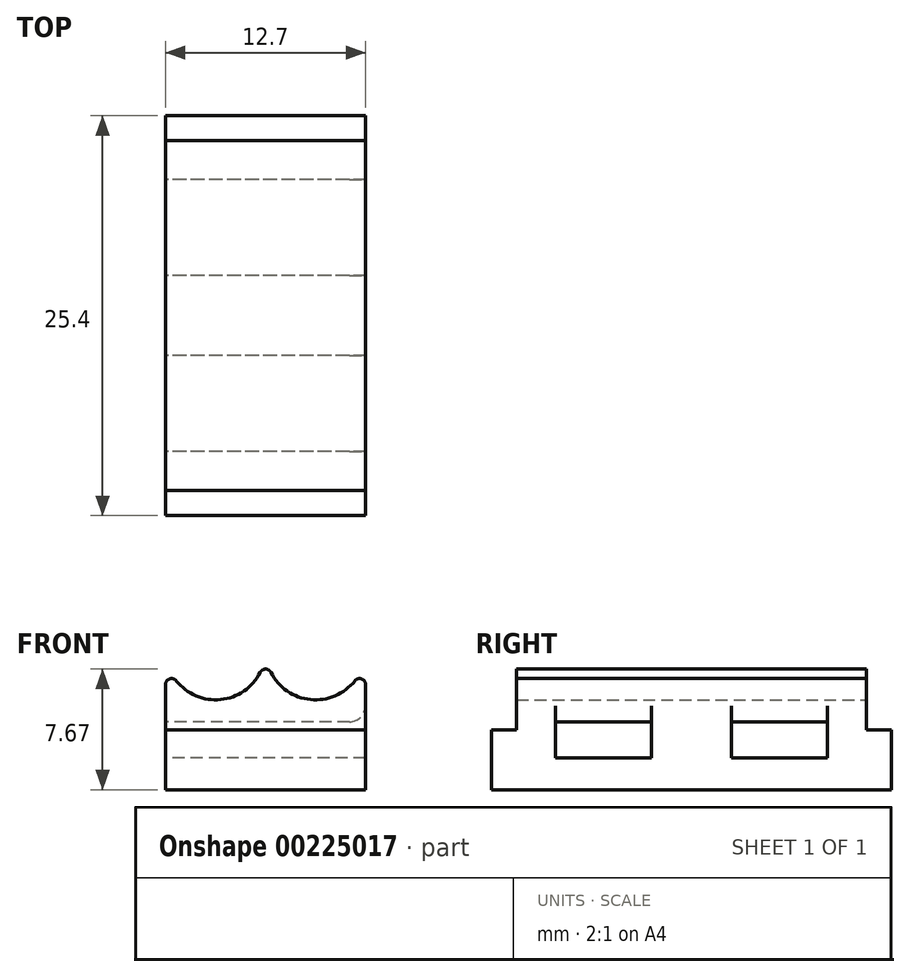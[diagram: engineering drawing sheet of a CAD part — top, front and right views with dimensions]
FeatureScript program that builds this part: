
annotation { "Feature Type Name" : "Feature", "Feature Type Description" : "" }
export const myFeature = defineFeature(function(context is Context, id is Id, definition is map)
    precondition{}
    {
        {
            var Q0;
            Q0=qCreatedBy(makeId("Top.planeOp"),FACE);
            var sketch = newSketch(context, id + "F0", { "sketchPlane" : qUnion([Q0])});
            skLineSegment(sketch, "E0.bottom", {"start": v(6.35, 12.7) * mm, "end": v(-6.35, 12.7) * mm});
            skLineSegment(sketch, "E0.top", {"start": v(6.35, -12.7) * mm, "end": v(-6.35, -12.7) * mm});
            skLineSegment(sketch, "E0.left", {"start": v(6.35, 12.7) * mm, "end": v(6.35, -12.7) * mm});
            skLineSegment(sketch, "E0.right", {"start": v(-6.35, 12.7) * mm, "end": v(-6.35, -12.7) * mm});
            skPoint(sketch, "E0.middle", {"position": v(0, 0) * mm});
            skSolve(sketch);
        }
        {
            var Q0;
            Q0=makeQuery(id+"F0.imprint","IMPRINT",FACE,{"disambiguationData":[TD([[makeQuery(id+"F0.imprint","IMPRINT",EDGE,{"derivedFrom":sQuery(id+"F0.wireOp",EDGE,"E0.bottom")}),1.0]])]});
            extrude(context, id + "F1", {"entities" : qUnion([Q0]), "depth" : 3.8 * mm});
        }
        {
            var Q0;
            Q0=qCreatedBy(makeId("Front.planeOp"),FACE);
            var sketch = newSketch(context, id + "F2", { "sketchPlane" : qUnion([Q0])});
            skArc(sketch, "E1", {"start": v(0, 8.9) * mm, "mid": v(3.18, 5.72) * mm, "end": v(6.35, 8.9) * mm});
            skLineSegment(sketch, "E2", {"start": v(6.35, 8.9) * mm, "end": v(6.35, 3.81) * mm});
            skPoint(sketch, "E3.0", {"position": v(6.35, 3.81) * mm});
            skArc(sketch, "E4.MirrorC", {"start": v(0, 8.9) * mm, "mid": v(-3.18, 5.72) * mm, "end": v(-6.35, 8.9) * mm});
            skLineSegment(sketch, "E5.MirrorCS", {"start": v(-6.35, 8.9) * mm, "end": v(-6.35, 3.81) * mm});
            skLineSegment(sketch, "E6", {"start": v(6.35, 3.81) * mm, "end": v(-6.35, 3.81) * mm});
            skSolve(sketch);
        }
        {
            var Q0;
            Q0=makeQuery(id+"F2.imprint","IMPRINT",FACE,{"disambiguationData":[TD([[makeQuery(id+"F2.imprint","IMPRINT",EDGE,{"derivedFrom":sQuery(id+"F2.wireOp",EDGE,"E1")}),-1.0]])]});
            extrude(context, id + "F3", {"entities" : qUnion([Q0]), "operationType" : NewBodyOperationType.ADD, "depth" : 22.22 * mm, "symmetric" : true});
        }
        {
            var Q0;
            Q0=makeQuery(id+"F3.boolean.opBoolean","MERGE",FACE,{"derivedFrom":[makeQuery(id+"F1.opExtrude","SWEPT_FACE",FACE,{"disambiguationData":[OSD([sQuery(id+"F0.wireOp",EDGE,"E0.right")])]}),makeQuery(id+"F3.opExtrude","SWEPT_FACE",FACE,{"disambiguationData":[OSD([sQuery(id+"F2.wireOp",EDGE,"c90f42b7-518b-497f-ae20-9e41afcd57c50.MirrorCS")])]})]});
            var sketch = newSketch(context, id + "F4", { "sketchPlane" : qUnion([Q0])});
            skLineSegment(sketch, "E7.bottom", {"start": v(-2.54, 2.03) * mm, "end": v(-8.64, 2.03) * mm});
            skLineSegment(sketch, "E7.top", {"start": v(-2.54, 4.32) * mm, "end": v(-8.64, 4.32) * mm});
            skLineSegment(sketch, "E7.left", {"start": v(-2.54, 2.03) * mm, "end": v(-2.54, 4.32) * mm});
            skLineSegment(sketch, "E7.right", {"start": v(-8.64, 2.03) * mm, "end": v(-8.64, 4.32) * mm});
            skPoint(sketch, "E7.middle", {"position": v(-5.59, 3.18) * mm});
            skLineSegment(sketch, "E8.MirrorCS", {"start": v(8.64, 2.03) * mm, "end": v(8.64, 4.32) * mm});
            skLineSegment(sketch, "E9.MirrorCS", {"start": v(2.54, 4.32) * mm, "end": v(8.64, 4.32) * mm});
            skLineSegment(sketch, "E10.MirrorCS", {"start": v(2.54, 2.03) * mm, "end": v(2.54, 4.32) * mm});
            skLineSegment(sketch, "E11.MirrorCS", {"start": v(2.54, 2.03) * mm, "end": v(8.64, 2.03) * mm});
            skSolve(sketch);
        }
        {
            var Q0;
            Q0=makeQuery(id+"F4.imprint","IMPRINT",FACE,{"disambiguationData":[TD([[makeQuery(id+"F4.imprint","IMPRINT",EDGE,{"derivedFrom":sQuery(id+"F4.wireOp",EDGE,"E7.bottom")}),-1.0]])]});
            var Q1;
            Q1=makeQuery(id+"F4.imprint","IMPRINT",FACE,{"disambiguationData":[TD([[makeQuery(id+"F4.imprint","IMPRINT",EDGE,{"derivedFrom":sQuery(id+"F4.wireOp",EDGE,"E8.MirrorCS")}),1.0]])]});
            extrude(context, id + "F5", {"entities" : qUnion([Q0, Q1]), "operationType" : NewBodyOperationType.REMOVE, "oppositeDirection" : true, "depth" : 25.4 * mm});
        }
        {
            var Q0;
            Q0=makeQuery(id+"F3.opExtrude","SWEPT_EDGE",EDGE,{"disambiguationData":[OSD([sQuery(id+"F2.wireOp",EDGE,"E1"),sQuery(id+"F2.wireOp",EDGE,"E2")])]});
            var Q1;
            Q1=makeQuery(id+"F3.opExtrude","SWEPT_EDGE",EDGE,{"disambiguationData":[OSD([sQuery(id+"F2.wireOp",EDGE,"E1"),sQuery(id+"F2.wireOp",EDGE,"E4.MirrorC")])]});
            var Q2;
            Q2=makeQuery(id+"F3.opExtrude","SWEPT_EDGE",EDGE,{"disambiguationData":[OSD([sQuery(id+"F2.wireOp",EDGE,"E4.MirrorC"),sQuery(id+"F2.wireOp",EDGE,"E5.MirrorCS")])]});
            fillet(context, id + "F6", {"entities" : qUnion([Q0, Q1, Q2]), "radius" : 0.38 * mm, "tangentPropagation" : true, "allowEdgeOverflow" : false});
        }
        {
            var Q0;
            Q0=makeQuery(id+"F5.boolean.opBoolean","INTERSECT",EDGE,{"derivedFrom":[makeQuery(id+"F3.boolean.opBoolean","MERGE",FACE,{"derivedFrom":[makeQuery(id+"F1.opExtrude","SWEPT_FACE",FACE,{"disambiguationData":[OSD([sQuery(id+"F0.wireOp",EDGE,"E0.left")])]}),makeQuery(id+"F3.opExtrude","SWEPT_FACE",FACE,{"disambiguationData":[OSD([sQuery(id+"F2.wireOp",EDGE,"E2")])]})]}),makeQuery(id+"F5.opExtrude","SWEPT_FACE",FACE,{"disambiguationData":[OSD([sQuery(id+"F4.wireOp",EDGE,"E7.top")])]})]});
            var Q1;
            Q1=makeQuery(id+"F5.boolean.opBoolean","INTERSECT",EDGE,{"derivedFrom":[makeQuery(id+"F3.boolean.opBoolean","MERGE",FACE,{"derivedFrom":[makeQuery(id+"F1.opExtrude","SWEPT_FACE",FACE,{"disambiguationData":[OSD([sQuery(id+"F0.wireOp",EDGE,"E0.left")])]}),makeQuery(id+"F3.opExtrude","SWEPT_FACE",FACE,{"disambiguationData":[OSD([sQuery(id+"F2.wireOp",EDGE,"E2")])]})]}),makeQuery(id+"F5.opExtrude","SWEPT_FACE",FACE,{"disambiguationData":[OSD([sQuery(id+"F4.wireOp",EDGE,"E9.MirrorCS")])]})]});
            var Q2;
            Q2=makeQuery(id+"F5.boolean.opBoolean","COPY",EDGE,{"derivedFrom":makeQuery(id+"F5.opExtrude","CAP_EDGE",EDGE,{"disambiguationData":[OSD([sQuery(id+"F4.wireOp",EDGE,"E9.MirrorCS")])],"isStart":true})});
            var Q3;
            Q3=makeQuery(id+"F5.boolean.opBoolean","COPY",EDGE,{"derivedFrom":makeQuery(id+"F5.opExtrude","CAP_EDGE",EDGE,{"disambiguationData":[OSD([sQuery(id+"F4.wireOp",EDGE,"E7.top")])],"isStart":true})});
            fillet(context, id + "F7", {"entities" : qUnion([Q0, Q1, Q2, Q3]), "radius" : 1.02 * mm, "tangentPropagation" : true, "allowEdgeOverflow" : false});
        }
    });
